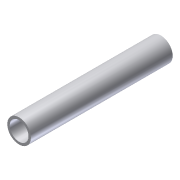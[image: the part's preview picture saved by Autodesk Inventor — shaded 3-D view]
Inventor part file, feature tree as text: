
AUTODESK INVENTOR PART (.ipt)
format: ipt  version: 2012 (Build 160160000, 160)  size: 77,312 bytes
history: native  units: in
note: dims shown in document units (in); Inventor stores cm internally (conversion verified against a paired STEP export)
features: extrude x1, sketch x1
ambient origin geometry x8: Origin, YZ Plane, XZ Plane, XY Plane, X Axis, Y Axis, Z Axis, Center Point
bodies: Solid1 (feature_tree)
feature tree (2):
  extrude  "Extrusion1"  Depth=1.592in
  sketch  "Sketch1"  dims[d0=2.0in d2=1.592in d3=12.0in d4=0.0in]
